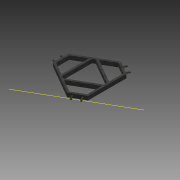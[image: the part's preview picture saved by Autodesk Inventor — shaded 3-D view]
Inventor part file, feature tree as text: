
AUTODESK INVENTOR PART (.ipt)
format: ipt  version: 2016 (Build 200138000, 138)  size: 175,616 bytes
history: native  units: in
note: dims shown in document units (in); Inventor stores cm internally (conversion verified against a paired STEP export)
features: projected_geometry x8, sketch x7, extrude x4, other x3, revolve x3
ambient origin geometry x8: Origin, YZ Plane, XZ Plane, XY Plane, X Axis, Y Axis, Z Axis, Center Point
bodies: Solid1 (feature_tree)
feature tree (25):
  extrude  "Extrusion1"  Depth=20.0in
  extrude  "Extrusion2"  Depth=15.5in
  extrude  "Extrusion3"  Depth=2.0in TaperAngle=0.0deg
  extrude  "Extrusion4"  Depth=2.0in
  sketch  "Sketch5"  dims[d25=0.75in d26=0.75in]
  other  "Work Axis2"
  revolve  "Revolution1"  [1 undecoded]
  sketch  "Sketch6"  dims[d27=2.0in d28=0.0in d29=2.0in]
  other  "Work Axis3"
  revolve  "Revolution2"  [1 undecoded]
  sketch  "Sketch7"  dims[d30=2.0in d31=0.75in d32=0.75in d33=2.0in d34=0.0in d35=2.0in d36=2.0in d37=0.75in d38=0.75in d39=2.0in d40=0.0in d47=90.0deg d50=90.0deg d53=90.0deg]
  other  "Work Axis4"
  revolve  "Revolution3"  [1 undecoded]
  sketch  "Sketch1"  dims[d0=8.0in d6=20.0in]
  sketch  "Sketch2"  dims[d14=15.5in d16=15.5in]
  projected_geometry  "Projected Loop1"
  sketch  "Sketch3"  dims[d17=15.5in d21=2.0in d22=0.0in]
  projected_geometry  "Projected Loop2"
  sketch  "Sketch4"  dims[d23=2.0in d24=2.0in]
  projected_geometry  "Projected Loop3"
  projected_geometry  "Projected Loop4"
  projected_geometry  "Projected Loop5"
  projected_geometry  "Projected Loop6"
  projected_geometry  "Projected Loop7"
  projected_geometry  "Projected Loop8"
note: 3 required parameter values undecoded (feature->parameter linkage not recoverable at this tier; creation-order binding heuristic only, values carry confidence <= 0.55)
